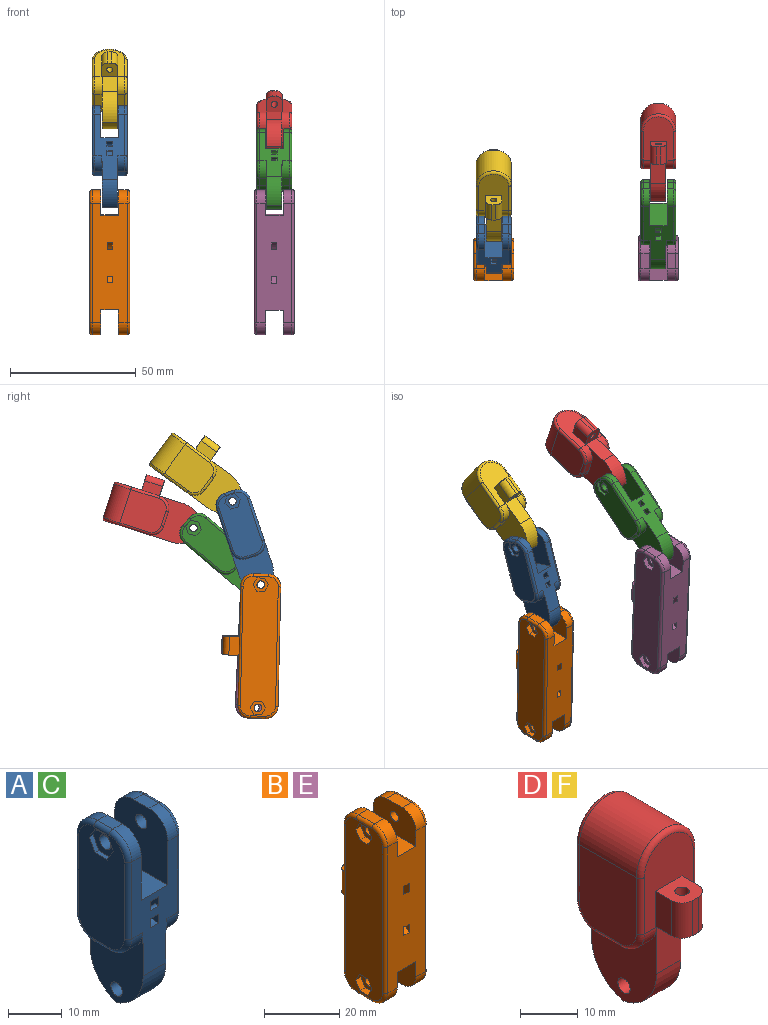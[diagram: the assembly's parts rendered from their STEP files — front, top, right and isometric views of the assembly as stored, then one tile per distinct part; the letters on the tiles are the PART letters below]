
ASSEMBLY  parts=6 mates=4
PART A: 67 faces, bbox 14x14.8x42.5 mm
  f0: plane 0.67x0.25mm, normal (0,0,-1), area 0.2mm2, adj f14,f15,f30,f57
  f1: plane 0.67x0.25mm, normal (0,0,-1), area 0.2mm2, adj f2,f14,f16,f26
  f2: plane 2.5x0.67mm, normal (-1,0,0), area 0.5mm2, adj f1,f16,f26
  f3: plane 2.5x0.67mm, normal (1,0,0), area 0.5mm2, adj f16,f29,f58
  f4: plane 25.5x12mm, normal (1,0,0), area 268.5mm2, adj f34,f35,f36,f37,f38,f39,f40,f41
  f5: plane 25.5x12mm, normal (-1,0,0), area 266.1mm2, adj f19,f20,f21,f22,f23,f24,f42,f43
  f6: plane 17.04x14mm, normal (1,0,0), area 170.6mm2, adj f7,f15,f16,f29,f33,f50,f53,f54
  f7: plane 4x3mm, normal (0,0,-1), area 12mm2, adj f6,f29,f33,f37
  f8: plane 4x2.5mm, normal (0,0,1), area 10mm2, adj f9,f28,f32,f38
  f9: plane 15x14mm, normal (-1,0,0), area 192.2mm2, adj f8,f10,f15,f16,f18,f28,f32
  f10: plane 14x7mm, normal (0,0,1), area 98mm2, adj f9,f11,f15,f16
  f11: plane 15x14mm, normal (1,0,0), area 192.2mm2, adj f10,f12,f15,f16,f17,f27,f31
  f12: plane 4x2.5mm, normal (0,0,1), area 10mm2, adj f11,f27,f31,f44
  f13: plane 4x3mm, normal (0,0,-1), area 12mm2, adj f14,f26,f30,f47
  f14: plane 17.04x14mm, normal (-1,0,0), area 170.6mm2, adj f0,f1,f13,f15,f16,f26,f30,f50
  f15: plane 27.5x12mm, normal (0,-1,0), area 192.1mm2, adj f0,f6,f9,f10,f11,f14,f30,f31
  f16: plane 27.5x12mm, normal (0,1,0), area 192.1mm2, adj f1,f2,f3,f6,f9,f10,f11,f14
  f17: cylinder r=1.5mm len=3mm, axis (-1,0,0), area 23.6mm2, adj f11,f25
  f18: cylinder r=1.5mm len=3mm, axis (-1,0,0), area 23.6mm2, adj f9,f52
  f19: plane 3.17x1mm, normal (0,0.03,-1), area 3.2mm2, adj f5,f20,f24,f25
  f20: plane 2.69x1.68mm, normal (0,-0.85,-0.53), area 3.2mm2, adj f5,f19,f21,f25
  f21: plane 2.8x1.49mm, normal (0,-0.88,0.47), area 3.2mm2, adj f5,f20,f22,f25
  f22: plane 3.17x1mm, normal (0,-0.03,1), area 3.2mm2, adj f5,f21,f23,f25
  f23: plane 2.69x1.68mm, normal (0,0.85,0.53), area 3.2mm2, adj f5,f22,f24,f25
  f24: plane 2.8x1.49mm, normal (0,0.88,-0.47), area 3.2mm2, adj f5,f19,f23,f25
  f25: plane 6.35x5.61mm, normal (-1,0,0), area 19.1mm2, adj f17,f19,f20,f21,f22,f23,f24
  f26: cylinder r=5mm len=5mm, axis (1,0,0), area 22.9mm2, adj f1,f2,f13,f14,f16,f45
  f27: cylinder r=5mm len=5mm, axis (-1,0,0), area 19.6mm2, adj f11,f12,f16,f42
  f28: cylinder r=5mm len=5mm, axis (-1,0,0), area 19.6mm2, adj f8,f9,f16,f36
  f29: cylinder r=5mm len=5mm, axis (1,0,0), area 22.9mm2, adj f3,f6,f7,f16,f35,f58
  f30: cylinder r=5mm len=5mm, axis (-1,0,0), area 22.9mm2, adj f0,f13,f14,f15,f49,f57
  f31: cylinder r=5mm len=5mm, axis (1,0,0), area 19.6mm2, adj f11,f12,f15,f46
  f32: cylinder r=5mm len=5mm, axis (1,0,0), area 19.6mm2, adj f8,f9,f15,f40
  f33: cylinder r=5mm len=5mm, axis (-1,0,0), area 22.9mm2, adj f6,f7,f15,f39,f55,f56
  f34: cylinder r=1mm len=17.5mm, axis (0,0,1), area 27.5mm2, adj f4,f16,f35,f36
  f35: torus R=4mm, axis (-1,0,0), area 11.4mm2, adj f4,f29,f34,f37
  f36: torus R=4mm, axis (-1,0,0), area 11.4mm2, adj f4,f28,f34,f38
  f37: cylinder r=1mm len=4mm, axis (0,1,0), area 6.3mm2, adj f4,f7,f35,f39
  f38: cylinder r=1mm len=4mm, axis (0,-1,0), area 6.3mm2, adj f4,f8,f36,f40
  f39: torus R=4mm, axis (-1,0,0), area 11.4mm2, adj f4,f33,f37,f41
  f40: torus R=4mm, axis (-1,0,0), area 11.4mm2, adj f4,f32,f38,f41
  f41: cylinder r=1mm len=17.5mm, axis (0,0,-1), area 27.5mm2, adj f4,f15,f39,f40
  f42: torus R=4mm, axis (-1,0,0), area 11.4mm2, adj f5,f27,f43,f44
  f43: cylinder r=1mm len=17.5mm, axis (0,0,-1), area 27.5mm2, adj f5,f16,f42,f45
  f44: cylinder r=1mm len=4mm, axis (0,1,0), area 6.3mm2, adj f5,f12,f42,f46
  f45: torus R=4mm, axis (-1,0,0), area 11.4mm2, adj f5,f26,f43,f47
  f46: torus R=4mm, axis (-1,0,0), area 11.4mm2, adj f5,f31,f44,f48
  f47: cylinder r=1mm len=4mm, axis (0,-1,0), area 6.3mm2, adj f5,f13,f45,f49
  f48: cylinder r=1mm len=17.5mm, axis (0,0,1), area 27.5mm2, adj f5,f15,f46,f49
  f49: torus R=4mm, axis (-1,0,0), area 11.4mm2, adj f5,f30,f47,f48
  f50: cylinder r=1.5mm len=6mm, axis (-1,0,0), area 56.5mm2, adj f6,f14
  f51: cylinder r=2.75mm len=5.5mm, axis (1,0,0), area 17.3mm2, adj f4,f52
  f52: plane 5.5x5.5mm, normal (1,0,0), area 16.7mm2, adj f18,f51
  f53: cylinder r=10mm len=9.54mm, axis (-1,0,0), area 76mm2, adj f6,f14,f15,f54
  f54: cylinder r=10mm len=9.54mm, axis (1,0,0), area 76mm2, adj f6,f14,f16,f53
  f55: plane 0.67x0.25mm, normal (0,0,-1), area 0.2mm2, adj f6,f15,f33,f56
  f56: plane 2.5x0.67mm, normal (1,0,0), area 0.5mm2, adj f15,f33,f55
  f57: plane 2.5x0.67mm, normal (-1,0,0), area 0.5mm2, adj f0,f15,f30
  f58: plane 0.67x0.25mm, normal (0,0,-1), area 0.2mm2, adj f3,f6,f16,f29
  f59: cylinder r=1.04mm len=2.2mm, axis (1,0,0), area 9.3mm2, adj f16,f61,f62
  f60: cylinder r=3.04mm len=6.07mm, axis (1,0,0), area 23mm2, adj f16,f61,f62
  f61: plane 6.07x3.5mm, normal (1,0,0), area 14.7mm2, adj f16,f59,f60
  f62: plane 6.07x3.5mm, normal (-1,0,0), area 14.7mm2, adj f16,f59,f60
  f63: cylinder r=3.04mm len=6.07mm, axis (1,0,0), area 23mm2, adj f15,f65,f66
  f64: cylinder r=1.04mm len=2.2mm, axis (1,0,0), area 9.3mm2, adj f15,f65,f66
  f65: plane 6.07x3.5mm, normal (1,0,0), area 14.7mm2, adj f15,f63,f64
  f66: plane 6.07x3.5mm, normal (-1,0,0), area 14.7mm2, adj f15,f63,f64
PART B: 72 faces, bbox 16x22.9x58.3 mm
  f0: plane 47.5x14mm, normal (0,-1,0), area 584.2mm2, adj f4,f5,f6,f9,f10,f11,f38,f39
  f1: plane 55.5x14mm, normal (-1,0,0), area 714.6mm2, adj f22,f23,f24,f25,f26,f27,f29,f30
  f2: plane 55.5x14mm, normal (1,0,0), area 715.7mm2, adj f14,f16,f44,f45,f46,f47,f48,f49
  f3: plane 6x3.5mm, normal (0,0,1), area 21mm2, adj f4,f37,f39,f44
  f4: plane 16x10mm, normal (-1,0,0), area 142.2mm2, adj f0,f3,f5,f13,f21,f37,f39
  f5: plane 16x7mm, normal (0,0,1), area 112mm2, adj f0,f4,f6,f13
  f6: plane 16x10mm, normal (1,0,0), area 142.2mm2, adj f0,f5,f7,f13,f20,f36,f38
  f7: plane 6x3.5mm, normal (0,0,1), area 21mm2, adj f6,f36,f38,f52
  f8: plane 6x3.5mm, normal (0,0,-1), area 21mm2, adj f9,f41,f43,f59
  f9: plane 16x10mm, normal (1,0,0), area 142.2mm2, adj f0,f8,f10,f13,f19,f41,f43
  f10: plane 16x7mm, normal (0,0,-1), area 112mm2, adj f0,f9,f11,f13
  f11: plane 16x10mm, normal (-1,0,0), area 142.2mm2, adj f0,f10,f12,f13,f18,f40,f42
  f12: plane 6x3.5mm, normal (0,0,-1), area 21mm2, adj f11,f40,f42,f51
  f13: plane 47.5x14mm, normal (0,1,0), area 546.3mm2, adj f4,f5,f6,f9,f10,f11,f36,f37
  f14: cylinder r=2.75mm len=5.5mm, axis (1,0,0), area 34.6mm2, adj f2,f15
  f15: plane 5.5x5.5mm, normal (1,0,0), area 16.7mm2, adj f14,f18
  f16: cylinder r=2.75mm len=5.5mm, axis (1,0,0), area 34.6mm2, adj f2,f17
  f17: plane 5.5x5.5mm, normal (1,0,0), area 16.7mm2, adj f16,f21
  f18: cylinder r=1.5mm len=3mm, axis (1,0,0), area 23.6mm2, adj f11,f15
  f19: cylinder r=1.5mm len=3mm, axis (1,0,0), area 23.6mm2, adj f9,f28
  f20: cylinder r=1.5mm len=3mm, axis (1,0,0), area 23.6mm2, adj f6,f35
  f21: cylinder r=1.5mm len=3mm, axis (1,0,0), area 23.6mm2, adj f4,f17
  f22: plane 2.67x2mm, normal (0,-0.87,-0.49), area 6.1mm2, adj f1,f23,f27,f28
  f23: plane 2.63x2mm, normal (0,-0.86,0.51), area 6.1mm2, adj f1,f22,f24,f28
  f24: plane 3.06x2mm, normal (0,0.01,1), area 6.1mm2, adj f1,f23,f25,f28
  f25: plane 2.67x2mm, normal (0,0.87,0.49), area 6.1mm2, adj f1,f24,f26,f28
  f26: plane 2.63x2mm, normal (0,0.86,-0.51), area 6.1mm2, adj f1,f25,f27,f28
  f27: plane 3.06x2mm, normal (0,-0.01,-1), area 6.1mm2, adj f1,f22,f26,f28
  f28: plane 6.12x5.34mm, normal (-1,0,0), area 17.3mm2, adj f19,f22,f23,f24,f25,f26,f27
  f29: plane 3.06x2mm, normal (0,-0.02,-1), area 6.1mm2, adj f1,f30,f34,f35
  f30: plane 2.68x2mm, normal (0,-0.87,-0.49), area 6.1mm2, adj f1,f29,f31,f35
  f31: plane 2.62x2mm, normal (0,-0.86,0.51), area 6.1mm2, adj f1,f30,f32,f35
  f32: plane 3.06x2mm, normal (0,0.02,1), area 6.1mm2, adj f1,f31,f33,f35
  f33: plane 2.68x2mm, normal (0,0.87,0.49), area 6.1mm2, adj f1,f32,f34,f35
  f34: plane 2.62x2mm, normal (0,0.86,-0.51), area 6.1mm2, adj f1,f29,f33,f35
  f35: plane 6.12x5.35mm, normal (-1,0,0), area 17.3mm2, adj f20,f29,f30,f31,f32,f33,f34
  f36: cylinder r=5mm len=5mm, axis (-1,0,0), area 27.5mm2, adj f6,f7,f13,f54
  f37: cylinder r=5mm len=5mm, axis (-1,0,0), area 27.5mm2, adj f3,f4,f13,f46
  f38: cylinder r=5mm len=5mm, axis (1,0,0), area 27.5mm2, adj f0,f6,f7,f53
  f39: cylinder r=5mm len=5mm, axis (1,0,0), area 27.5mm2, adj f0,f3,f4,f45
  f40: cylinder r=5mm len=5mm, axis (1,0,0), area 27.5mm2, adj f11,f12,f13,f50
  f41: cylinder r=5mm len=5mm, axis (1,0,0), area 27.5mm2, adj f8,f9,f13,f58
  f42: cylinder r=5mm len=5mm, axis (-1,0,0), area 27.5mm2, adj f0,f11,f12,f49
  f43: cylinder r=5mm len=5mm, axis (-1,0,0), area 27.5mm2, adj f0,f8,f9,f57
  f44: cylinder r=1mm len=6mm, axis (0,1,0), area 9.4mm2, adj f2,f3,f45,f46
  f45: torus R=4mm, axis (-1,0,0), area 11.4mm2, adj f2,f39,f44,f47
  f46: torus R=4mm, axis (-1,0,0), area 11.4mm2, adj f2,f37,f44,f48
  f47: cylinder r=1mm len=47.5mm, axis (0,0,-1), area 74.6mm2, adj f0,f2,f45,f49
  f48: cylinder r=1mm len=47.5mm, axis (0,0,1), area 74.6mm2, adj f2,f13,f46,f50
  f49: torus R=4mm, axis (-1,0,0), area 11.4mm2, adj f2,f42,f47,f51
  f50: torus R=4mm, axis (-1,0,0), area 11.4mm2, adj f2,f40,f48,f51
  f51: cylinder r=1mm len=6mm, axis (0,-1,0), area 9.4mm2, adj f2,f12,f49,f50
  f52: cylinder r=1mm len=6mm, axis (0,-1,0), area 9.4mm2, adj f1,f7,f53,f54
  f53: torus R=4mm, axis (-1,0,0), area 11.4mm2, adj f1,f38,f52,f55
  f54: torus R=4mm, axis (-1,0,0), area 11.4mm2, adj f1,f36,f52,f56
  f55: cylinder r=1mm len=47.5mm, axis (0,0,1), area 74.6mm2, adj f0,f1,f53,f57
  f56: cylinder r=1mm len=47.5mm, axis (0,0,-1), area 74.6mm2, adj f1,f13,f54,f58
  f57: torus R=4mm, axis (-1,0,0), area 11.4mm2, adj f1,f43,f55,f59
  f58: torus R=4mm, axis (-1,0,0), area 11.4mm2, adj f1,f41,f56,f59
  f59: cylinder r=1mm len=6mm, axis (0,1,0), area 9.4mm2, adj f1,f8,f57,f58
  f60: plane 6.5x6.5mm, normal (0,0,-1), area 34.7mm2, adj f13,f61,f63,f64,f65,f66,f67
  f61: plane 7.5x4mm, normal (1,0,0), area 30mm2, adj f13,f60,f62,f66
  f62: plane 6.5x6.5mm, normal (0,0,1), area 34.7mm2, adj f13,f61,f63,f64,f65,f66,f67
  f63: plane 7.5x4mm, normal (-1,0,0), area 30mm2, adj f13,f60,f62,f67
  f64: plane 7.5x1.5mm, normal (0,1,0), area 11.2mm2, adj f60,f62,f66,f67
  f65: cylinder r=1.25mm len=7.5mm, axis (0,0,1), area 58.9mm2, adj f60,f62
  f66: cylinder r=2.5mm len=7.5mm, axis (0,0,1), area 29.5mm2, adj f60,f61,f62,f64
  f67: cylinder r=2.5mm len=7.5mm, axis (0,0,-1), area 29.5mm2, adj f60,f62,f63,f64
  f68: cylinder r=8mm len=10.58mm, axis (1,0,0), area 23.1mm2, adj f0,f70,f71
  f69: cylinder r=10mm len=16mm, axis (1,0,0), area 37.1mm2, adj f0,f70,f71
  f70: plane 16x4mm, normal (1,0,0), area 30.2mm2, adj f0,f68,f69
  f71: plane 16x4mm, normal (-1,0,0), area 30.2mm2, adj f0,f68,f69
PART C: same geometry as A
PART D: 40 faces, bbox 15.2x22.9x39.3 mm
  f0: plane 27.97x12mm, normal (0,1,0), area 251.2mm2, adj f1,f7,f10,f11,f14,f15,f16,f27
  f1: plane 19.8x16mm, normal (1,0,0), area 201mm2, adj f0,f2,f8,f9,f11,f13,f26,f27
  f2: plane 6x3mm, normal (0,0,-1), area 18mm2, adj f1,f11,f13,f19
  f3: plane 15.97x14mm, normal (1,0,0), area 216.7mm2, adj f4,f15,f17,f19,f21,f23
  f4: cylinder r=7mm len=14mm, axis (0,1,0), area 307.9mm2, adj f3,f5,f14,f25
  f5: plane 15.97x14mm, normal (-1,0,0), area 216.7mm2, adj f4,f16,f18,f20,f22,f24
  f6: plane 6x3mm, normal (0,0,-1), area 18mm2, adj f7,f10,f12,f20
  f7: plane 19.8x16mm, normal (-1,0,0), area 201mm2, adj f0,f6,f8,f9,f10,f12,f26,f27
  f8: plane 27.97x12mm, normal (0,-1,0), area 211.5mm2, adj f1,f7,f12,f13,f23,f24,f25,f26
  f9: cylinder r=1.5mm len=6mm, axis (1,0,0), area 56.5mm2, adj f1,f7
  f10: cylinder r=5mm len=5mm, axis (1,0,0), area 23.6mm2, adj f0,f6,f7,f18
  f11: cylinder r=5mm len=5mm, axis (1,0,0), area 23.6mm2, adj f0,f1,f2,f17
  f12: cylinder r=5mm len=5mm, axis (-1,0,0), area 23.6mm2, adj f6,f7,f8,f22
  f13: cylinder r=5mm len=5mm, axis (-1,0,0), area 23.6mm2, adj f1,f2,f8,f21
  f14: torus R=6mm, axis (0,-1,0), area 32.8mm2, adj f0,f4,f15,f16
  f15: cylinder r=1mm len=11.97mm, axis (0,0,1), area 18.8mm2, adj f0,f3,f14,f17
  f16: cylinder r=1mm len=11.97mm, axis (0,0,-1), area 18.8mm2, adj f0,f5,f14,f18
  f17: torus R=4mm, axis (1,0,0), area 11.4mm2, adj f3,f11,f15,f19
  f18: torus R=4mm, axis (1,0,0), area 11.4mm2, adj f5,f10,f16,f20
  f19: cylinder r=1mm len=6mm, axis (0,1,0), area 9.4mm2, adj f2,f3,f17,f21
  f20: cylinder r=1mm len=6mm, axis (0,-1,0), area 9.4mm2, adj f5,f6,f18,f22
  f21: torus R=4mm, axis (1,0,0), area 11.4mm2, adj f3,f13,f19,f23
  f22: torus R=4mm, axis (1,0,0), area 11.4mm2, adj f5,f12,f20,f24
  f23: cylinder r=1mm len=11.97mm, axis (0,0,-1), area 18.8mm2, adj f3,f8,f21,f25
  f24: cylinder r=1mm len=11.97mm, axis (0,0,1), area 18.8mm2, adj f5,f8,f22,f25
  f25: torus R=6mm, axis (0,-1,0), area 32.8mm2, adj f4,f8,f23,f24
  f26: cylinder r=10mm len=9.8mm, axis (-1,0,0), area 82.2mm2, adj f1,f7,f8,f27
  f27: cylinder r=10mm len=9.8mm, axis (1,0,0), area 82.2mm2, adj f0,f1,f7,f26
  f28: plane 7.5x1.5mm, normal (0,-1,0), area 11.3mm2, adj f30,f32,f34,f35
  f29: plane 7.5x4mm, normal (1,0,0), area 30mm2, adj f8,f30,f32,f34
  f30: plane 6.5x6.5mm, normal (0,0,1), area 34.7mm2, adj f8,f28,f29,f31,f33,f34,f35
  f31: plane 7.5x4mm, normal (-1,0,0), area 30mm2, adj f8,f30,f32,f35
  f32: plane 6.5x6.5mm, normal (0,0,-1), area 34.7mm2, adj f8,f28,f29,f31,f33,f34,f35
  f33: cylinder r=1.25mm len=7.5mm, axis (0,0,1), area 58.9mm2, adj f30,f32
  f34: cylinder r=2.5mm len=7.5mm, axis (0,0,-1), area 29.5mm2, adj f28,f29,f30,f32
  f35: cylinder r=2.5mm len=7.5mm, axis (0,0,1), area 29.5mm2, adj f28,f30,f31,f32
  f36: cylinder r=4.5mm len=7.48mm, axis (1,0,0), area 17.7mm2, adj f0,f38,f39
  f37: cylinder r=6.5mm len=12mm, axis (1,0,0), area 30.6mm2, adj f0,f38,f39
  f38: plane 12x4mm, normal (1,0,0), area 24.2mm2, adj f0,f36,f37
  f39: plane 12x4mm, normal (-1,0,0), area 24.2mm2, adj f0,f36,f37
PART E: same geometry as B
PART F: same geometry as D
PLACE A rot(axis=(-1,0,0),18.7deg) t=(-65.6,-69.83,57.35)mm
PLACE B rot(axis=(1,0,0),1.3deg) t=(-65.6,-74.96,16.05)mm
PLACE C rot(axis=(-1,0,0),50deg) t=(-0.12,-62.01,51.98)mm
PLACE D rot(axis=(-1,0,0),72.2deg) t=(-0.12,-36.9,66.88)mm
PLACE E rot(axis=(1,0,0),2.6deg) t=(-0.12,-74.51,16.09)mm
PLACE F rot(axis=(-1,0,0),53.7deg) t=(-65.6,-54.24,81.09)mm
MATE revolute B.f16 <-> A.f50  axis (1,0,0) through (-69.1,-75.52,40.54)mm
MATE revolute F.f9 <-> A.f51  axis (-1,0,0) through (-68.6,-64.3,73.69)mm
MATE revolute E.f16 <-> C.f50  axis (1,0,0) through (-3.62,-75.6,40.57)mm
MATE revolute D.f9 <-> C.f51  axis (-1,0,0) through (-3.12,-48.79,63.06)mm
